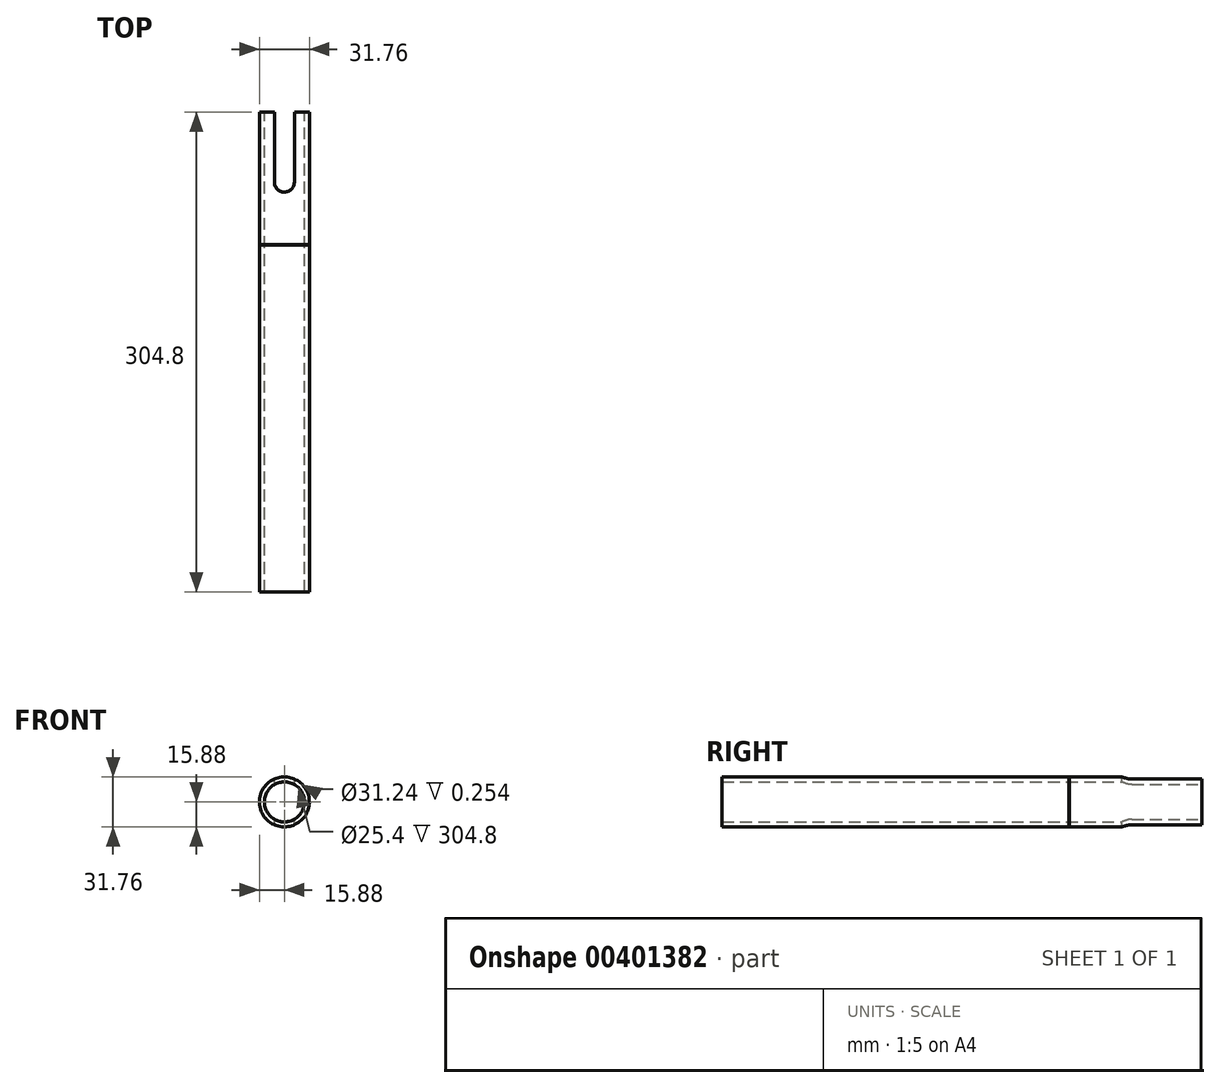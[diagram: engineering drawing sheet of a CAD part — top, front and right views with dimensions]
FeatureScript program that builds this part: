
annotation { "Feature Type Name" : "Feature", "Feature Type Description" : "" }
export const myFeature = defineFeature(function(context is Context, id is Id, definition is map)
    precondition{}
    {
        {
            var Q0;
            Q0=qCreatedBy(makeId("Front.planeOp"),FACE);
            var sketch = newSketch(context, id + "F0", { "sketchPlane" : qUnion([Q0])});
            skCircle(sketch, "E0", {"center": v(0, 0) * mm, "radius": 15.88 * mm});
            skCircle(sketch, "E1", {"center": v(0, 0) * mm, "radius": 12.7 * mm});
            skSolve(sketch);
        }
        {
            var Q0;
            Q0 = qSketchRegion(id + "F0", true);
            extrude(context, id + "F1", {"entities" : qUnion([Q0]), "depth" : 304.8 * mm});
        }
        {
            var Q0;
            Q0=qCreatedBy(makeId("Top.planeOp"),FACE);
            var sketch = newSketch(context, id + "F2", { "sketchPlane" : qUnion([Q0])});
            skLineSegment(sketch, "E2", {"start": v(-6.35, 0) * mm, "end": v(6.35, 0) * mm});
            skLineSegment(sketch, "E3", {"start": v(6.35, 0) * mm, "end": v(6.35, -44.45) * mm});
            skLineSegment(sketch, "E4", {"start": v(-6.35, 0) * mm, "end": v(-6.35, -44.45) * mm});
            skArc(sketch, "E5", {"start": v(-6.35, -44.45) * mm, "mid": v(0, -50.8) * mm, "end": v(6.35, -44.45) * mm});
            skSolve(sketch);
        }
        {
            var Q0;
            Q0 = qSketchRegion(id + "F2", true);
            extrude(context, id + "F3", {"entities" : qUnion([Q0]), "operationType" : NewBodyOperationType.REMOVE, "endBound" : BoundingType.SYMMETRIC, "oppositeDirection" : true, "depth" : 50.8 * mm});
        }
        {
            var Q0;
            Q0=qCreatedBy(makeId("Right.planeOp"),FACE);
            var sketch = newSketch(context, id + "F4", { "sketchPlane" : qUnion([Q0])});
            skLineSegment(sketch, "E6", {"start": v(0, 0) * mm, "end": v(-84.14, 0) * mm, "construction": true});
            skLineSegment(sketch, "E7.bottom", {"start": v(-84.4, -15.87) * mm, "end": v(-84.14, -15.87) * mm});
            skLineSegment(sketch, "E7.top", {"start": v(-84.4, -15.62) * mm, "end": v(-84.14, -15.62) * mm});
            skLineSegment(sketch, "E7.left", {"start": v(-84.4, -15.87) * mm, "end": v(-84.4, -15.62) * mm});
            skLineSegment(sketch, "E7.right", {"start": v(-84.14, -15.87) * mm, "end": v(-84.14, -15.62) * mm});
            skSolve(sketch);
        }
        {
            var Q0;
            Q0 = qSketchRegion(id + "F4", true);
            var Q1;
            Q1=sQuery(id+"F4.wireOp",EDGE,"E6");
            revolve(context, id + "F5", {"entities" : qUnion([Q0]), "axis" : qUnion([Q1]), "revolveType" : RevolveType.FULL});
        }
    });
